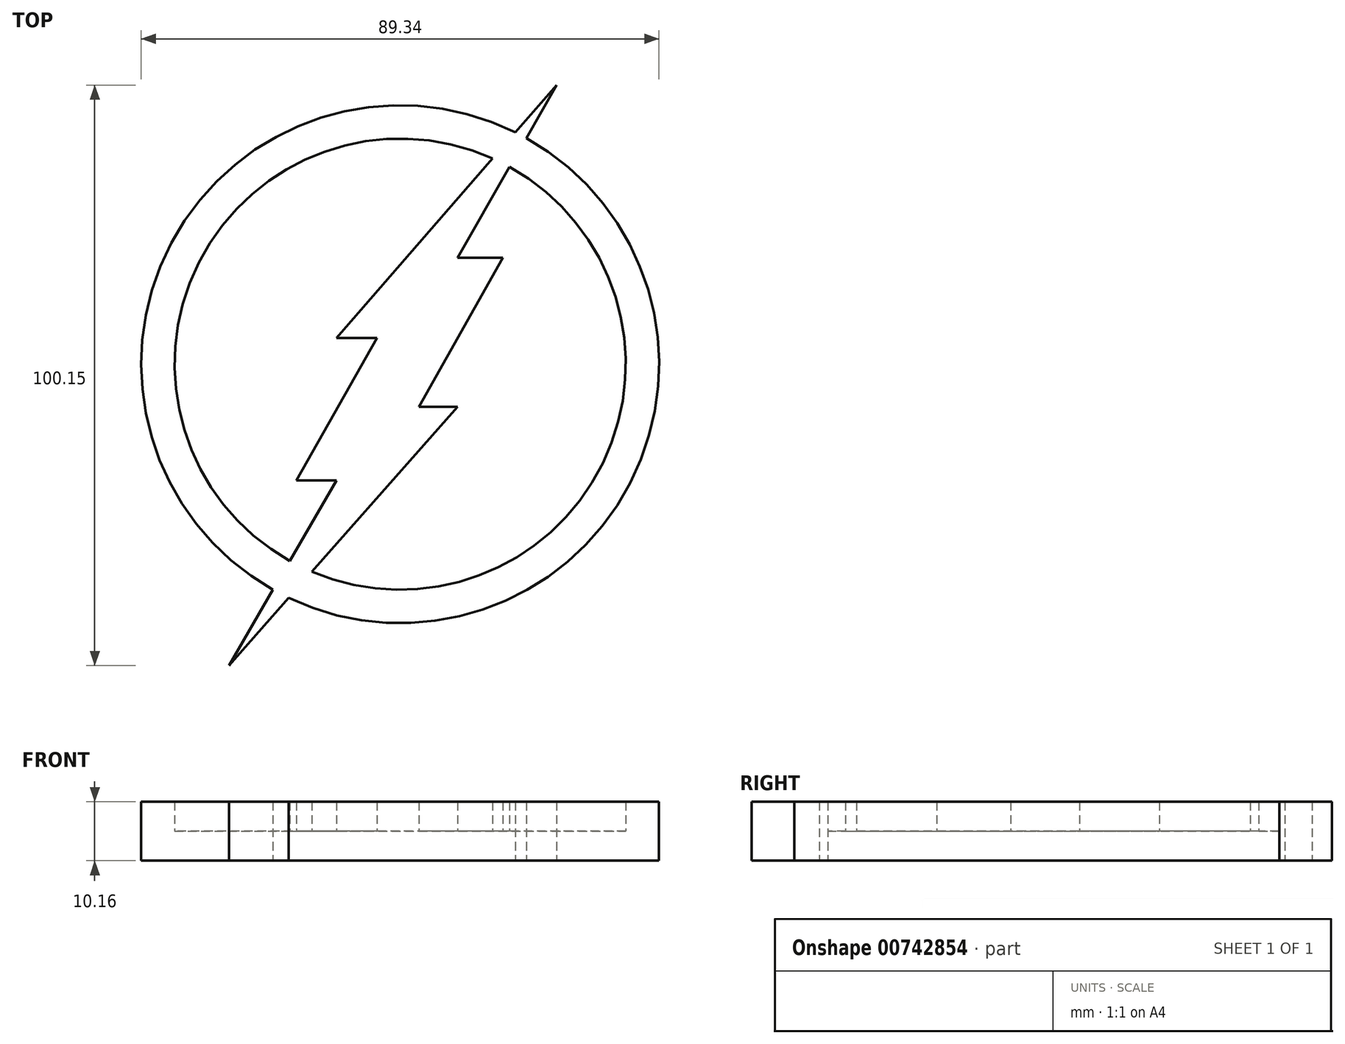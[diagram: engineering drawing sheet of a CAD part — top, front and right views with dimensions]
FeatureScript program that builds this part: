
annotation { "Feature Type Name" : "Feature", "Feature Type Description" : "" }
export const myFeature = defineFeature(function(context is Context, id is Id, definition is map)
    precondition{}
    {
        {
            var Q0;
            Q0=qCreatedBy(makeId("Top.planeOp"),FACE);
            var sketch = newSketch(context, id + "F0", { "sketchPlane" : qUnion([Q0])});
            skCircle(sketch, "E0", {"center": v(0, 0) * mm, "radius": 44.67 * mm});
            skCircle(sketch, "E1", {"center": v(0, 0) * mm, "radius": 38.92 * mm});
            skLineSegment(sketch, "E2", {"start": v(-29.55, -52) * mm, "end": v(9.94, -7.36) * mm});
            skLineSegment(sketch, "E3", {"start": v(9.94, -7.36) * mm, "end": v(3.23, -7.36) * mm});
            skLineSegment(sketch, "E4", {"start": v(3.23, -7.36) * mm, "end": v(17.73, 18.34) * mm});
            skLineSegment(sketch, "E5", {"start": v(17.73, 18.34) * mm, "end": v(9.94, 18.34) * mm});
            skLineSegment(sketch, "E6", {"start": v(26.97, 48.14) * mm, "end": v(-10.97, 4.52) * mm});
            skLineSegment(sketch, "E7", {"start": v(-10.97, 4.52) * mm, "end": v(-4, 4.52) * mm});
            skLineSegment(sketch, "E8", {"start": v(-4, 4.52) * mm, "end": v(-17.88, -20.07) * mm});
            skLineSegment(sketch, "E9", {"start": v(-17.88, -20.07) * mm, "end": v(-10.97, -20.07) * mm});
            skLineSegment(sketch, "E10", {"start": v(26.97, 48.14) * mm, "end": v(9.94, 18.34) * mm});
            skLineSegment(sketch, "E11", {"start": v(-29.55, -52) * mm, "end": v(-10.97, -20.07) * mm});
            skSolve(sketch);
        }
        {
            var Q0;
            {var subQ0=sQuery(id+"F0.wireOp",EDGE,"E6");var subQ1=sQuery(id+"F0.wireOp",EDGE,"E0");var subQ2=makeQuery(id+"F0.imprint","INTERSECT",VERTEX,{"derivedFrom":[subQ1,subQ0]});Q0=makeQuery(id+"F0.imprint","IMPRINT",FACE,{"disambiguationData":[TD([[makeQuery(id+"F0.imprint","IMPRINT",EDGE,{"disambiguationData":[TD([[subQ2,1.0]])],"derivedFrom":subQ1}),-1.0]])]});}
            var Q1;
            {var subQ0=sQuery(id+"F0.wireOp",EDGE,"E11");var subQ1=sQuery(id+"F0.wireOp",EDGE,"E0");var subQ2=makeQuery(id+"F0.imprint","INTERSECT",VERTEX,{"derivedFrom":[subQ1,subQ0]});Q1=makeQuery(id+"F0.imprint","IMPRINT",FACE,{"disambiguationData":[TD([[makeQuery(id+"F0.imprint","IMPRINT",EDGE,{"disambiguationData":[TD([[subQ2,-1.0]])],"derivedFrom":subQ1}),-1.0]])]});}
            var Q2;
            {var subQ0=sQuery(id+"F0.wireOp",EDGE,"E10");var subQ1=sQuery(id+"F0.wireOp",EDGE,"E0");var subQ2=makeQuery(id+"F0.imprint","INTERSECT",VERTEX,{"derivedFrom":[subQ1,subQ0]});Q2=makeQuery(id+"F0.imprint","IMPRINT",FACE,{"disambiguationData":[TD([[makeQuery(id+"F0.imprint","IMPRINT",EDGE,{"disambiguationData":[TD([[subQ2,1.0]])],"derivedFrom":subQ1}),1.0]])]});}
            var Q3;
            {var subQ0=sQuery(id+"F0.wireOp",EDGE,"E6");var subQ1=sQuery(id+"F0.wireOp",EDGE,"E0");var subQ2=makeQuery(id+"F0.imprint","INTERSECT",VERTEX,{"derivedFrom":[subQ1,subQ0]});Q3=makeQuery(id+"F0.imprint","IMPRINT",FACE,{"disambiguationData":[TD([[makeQuery(id+"F0.imprint","IMPRINT",EDGE,{"disambiguationData":[TD([[subQ2,1.0]])],"derivedFrom":subQ1}),1.0]])]});}
            var Q4;
            {var subQ0=sQuery(id+"F0.wireOp",EDGE,"E11");var subQ1=sQuery(id+"F0.wireOp",EDGE,"E0");var subQ2=makeQuery(id+"F0.imprint","INTERSECT",VERTEX,{"derivedFrom":[subQ1,subQ0]});Q4=makeQuery(id+"F0.imprint","IMPRINT",FACE,{"disambiguationData":[TD([[makeQuery(id+"F0.imprint","IMPRINT",EDGE,{"disambiguationData":[TD([[subQ2,-1.0]])],"derivedFrom":subQ1}),1.0]])]});}
            var Q5;
            {var subQ12=sQuery(id+"F0.wireOp",EDGE,"E3");Q5=makeQuery(id+"F0.imprint","IMPRINT",FACE,{"disambiguationData":[TD([[makeQuery(id+"F0.imprint","IMPRINT",EDGE,{"derivedFrom":subQ12}),1.0]])]});}
            var Q6;
            {var subQ0=sQuery(id+"F0.wireOp",EDGE,"E6");var subQ1=sQuery(id+"F0.wireOp",EDGE,"E0");var subQ2=makeQuery(id+"F0.imprint","INTERSECT",VERTEX,{"derivedFrom":[subQ1,subQ0]});Q6=makeQuery(id+"F0.imprint","IMPRINT",FACE,{"disambiguationData":[TD([[makeQuery(id+"F0.imprint","IMPRINT",EDGE,{"disambiguationData":[TD([[subQ2,-1.0]])],"derivedFrom":subQ1}),1.0]])]});}
            extrude(context, id + "F1", {"entities" : qUnion([Q0, Q1, Q2, Q3, Q4, Q5, Q6]), "depth" : 10.16 * mm, "offsetDistance" : 25.4 * mm});
        }
        {
            var Q0;
            {var subQ0=sQuery(id+"F0.wireOp",EDGE,"E7");Q0=makeQuery(id+"F0.imprint","IMPRINT",FACE,{"disambiguationData":[TD([[makeQuery(id+"F0.imprint","IMPRINT",EDGE,{"derivedFrom":subQ0}),-1.0]])]});}
            var Q1;
            {var subQ0=sQuery(id+"F0.wireOp",EDGE,"E3");Q1=makeQuery(id+"F0.imprint","IMPRINT",FACE,{"disambiguationData":[TD([[makeQuery(id+"F0.imprint","IMPRINT",EDGE,{"derivedFrom":subQ0}),-1.0]])]});}
            extrude(context, id + "F2", {"entities" : qUnion([Q0, Q1]), "operationType" : NewBodyOperationType.ADD, "depth" : 5.08 * mm, "offsetDistance" : 25.4 * mm});
        }
    });
